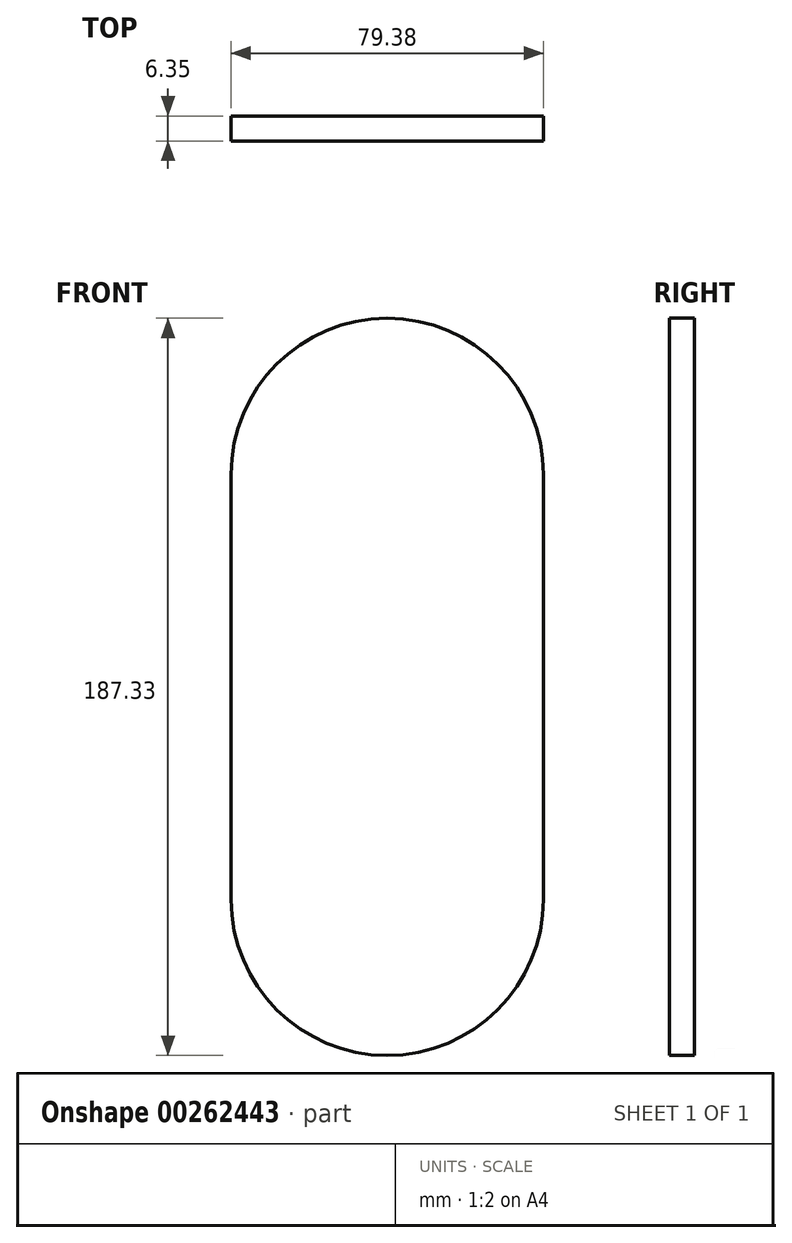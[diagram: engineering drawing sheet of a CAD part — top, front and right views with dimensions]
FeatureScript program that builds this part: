
annotation { "Feature Type Name" : "Feature", "Feature Type Description" : "" }
export const myFeature = defineFeature(function(context is Context, id is Id, definition is map)
    precondition{}
    {
        {
            var Q0;
            Q0=qCreatedBy(makeId("Front.planeOp"),FACE);
            var sketch = newSketch(context, id + "F0", { "sketchPlane" : qUnion([Q0])});
            skLineSegment(sketch, "E0", {"start": v(0, 32.52) * mm, "end": v(0, -75.43) * mm});
            skArc(sketch, "E1.0.startCap", {"start": v(-39.69, 32.52) * mm, "mid": v(0, 72.2) * mm, "end": v(39.69, 32.52) * mm});
            skArc(sketch, "E1.0.endCap", {"start": v(39.69, -75.43) * mm, "mid": v(0, -115.12) * mm, "end": v(-39.69, -75.43) * mm});
            skLineSegment(sketch, "E1.0.left", {"start": v(39.69, 32.52) * mm, "end": v(39.69, -75.43) * mm});
            skLineSegment(sketch, "E1.0.right", {"start": v(-39.69, 32.52) * mm, "end": v(-39.69, -75.43) * mm});
            skSolve(sketch);
        }
        {
            var Q0;
            Q0 = qSketchRegion(id + "F0", true);
            extrude(context, id + "F1", {"entities" : qUnion([Q0]), "depth" : 6.35 * mm});
        }
    });
